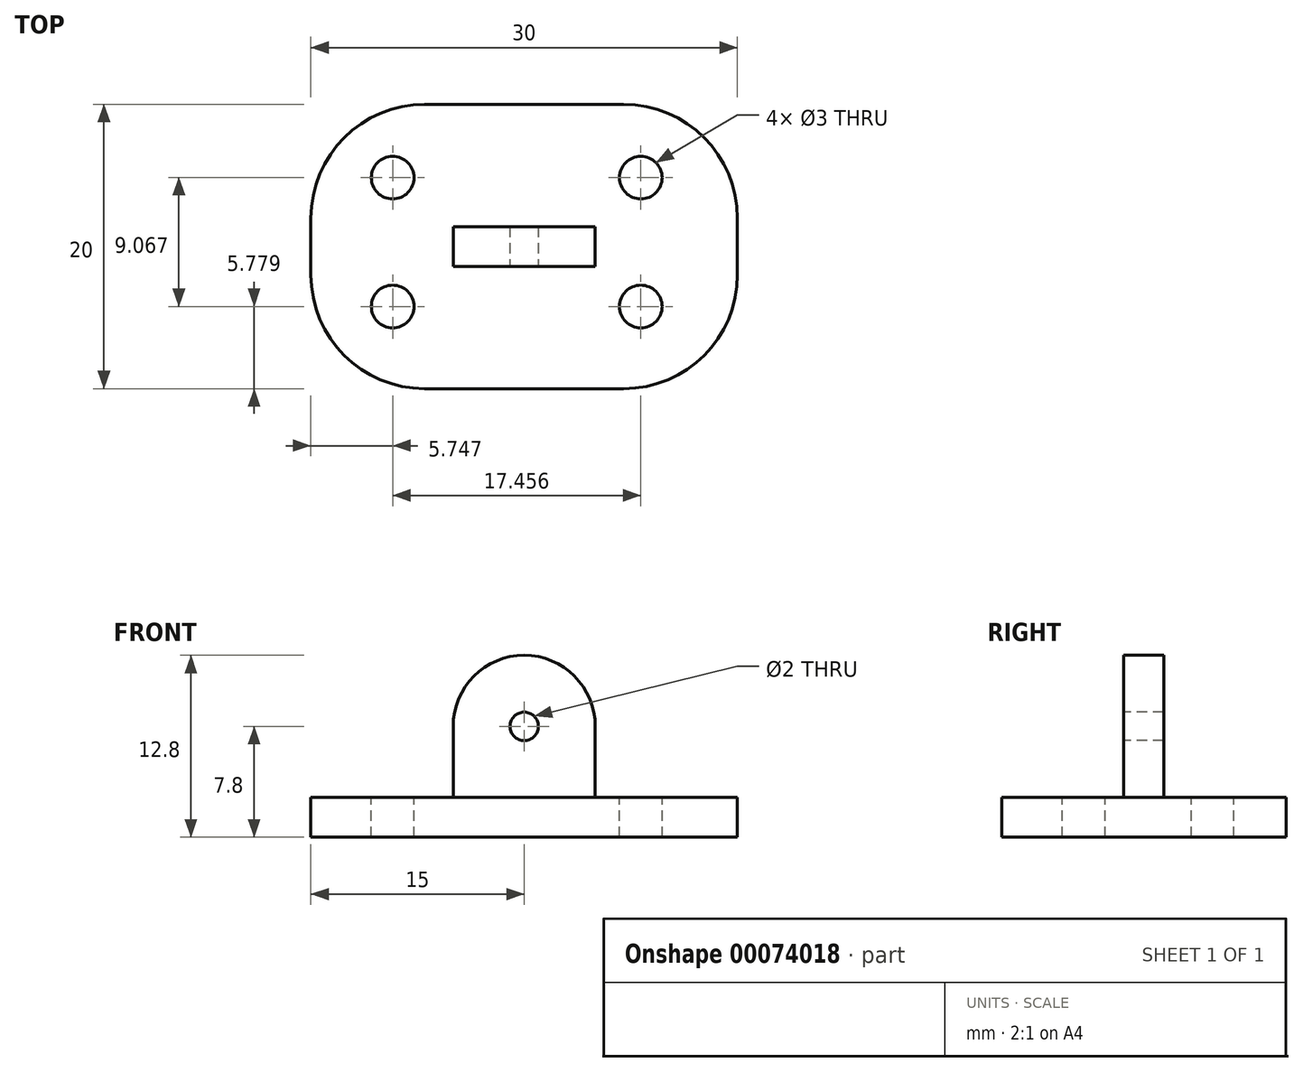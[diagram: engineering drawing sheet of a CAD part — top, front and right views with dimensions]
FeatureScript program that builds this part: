
annotation { "Feature Type Name" : "Feature", "Feature Type Description" : "" }
export const myFeature = defineFeature(function(context is Context, id is Id, definition is map)
    precondition{}
    {
        {
            var Q0;
            Q0=qCreatedBy(makeId("Top.planeOp"),FACE);
            var sketch = newSketch(context, id + "F0", { "sketchPlane" : qUnion([Q0])});
            skLineSegment(sketch, "E0.bottom", {"start": v(0, 0) * mm, "end": v(30, 0) * mm});
            skLineSegment(sketch, "E0.top", {"start": v(0, 20) * mm, "end": v(30, 20) * mm});
            skLineSegment(sketch, "E0.left", {"start": v(0, 0) * mm, "end": v(0, 20) * mm});
            skLineSegment(sketch, "E0.right", {"start": v(30, 0) * mm, "end": v(30, 20) * mm});
            skLineSegment(sketch, "E1.bottom", {"start": v(12.5, 11.4) * mm, "end": v(17.5, 11.4) * mm});
            skLineSegment(sketch, "E1.top", {"start": v(12.5, 8.6) * mm, "end": v(17.5, 8.6) * mm});
            skLineSegment(sketch, "E1.left", {"start": v(12.5, 11.4) * mm, "end": v(12.5, 8.6) * mm});
            skLineSegment(sketch, "E1.right", {"start": v(17.5, 11.4) * mm, "end": v(17.5, 8.6) * mm});
            skPoint(sketch, "E2", {"position": v(15, 20) * mm});
            skPoint(sketch, "E3", {"position": v(15, 11.4) * mm});
            skPoint(sketch, "E4", {"position": v(17.5, 10) * mm});
            skPoint(sketch, "E5", {"position": v(30, 10) * mm});
            skSolve(sketch);
        }
        {
            var Q0;
            Q0 = qSketchRegion(id + "F0", true);
            extrude(context, id + "F1", {"entities" : qUnion([Q0]), "depth" : 2.8 * mm, "offsetDistance" : 25 * mm});
        }
        {
            var Q0;
            Q0=makeQuery(id+"F1.opExtrude","CAP_FACE",FACE,{"disambiguationData":[OSD([sQuery(id+"F0.wireOp",EDGE,"E0.bottom"),sQuery(id+"F0.wireOp",EDGE,"E0.top"),sQuery(id+"F0.wireOp",EDGE,"E0.left"),sQuery(id+"F0.wireOp",EDGE,"E0.right"),sQuery(id+"F0.wireOp",EDGE,"E1.bottom"),sQuery(id+"F0.wireOp",EDGE,"E1.top"),sQuery(id+"F0.wireOp",EDGE,"E1.left"),sQuery(id+"F0.wireOp",EDGE,"E1.right")])],"isStart":false});
            var sketch = newSketch(context, id + "F2", { "sketchPlane" : qUnion([Q0])});
            skLineSegment(sketch, "E6.bottom", {"start": v(10, 11.4) * mm, "end": v(20, 11.4) * mm});
            skLineSegment(sketch, "E6.top", {"start": v(10, 8.6) * mm, "end": v(20, 8.6) * mm});
            skLineSegment(sketch, "E6.left", {"start": v(10, 11.4) * mm, "end": v(10, 8.6) * mm});
            skLineSegment(sketch, "E6.right", {"start": v(20, 11.4) * mm, "end": v(20, 8.6) * mm});
            skPoint(sketch, "E7", {"position": v(15, 11.4) * mm});
            skSolve(sketch);
        }
        {
            var Q0;
            {var subQ2=sQuery(id+"F2.wireOp",EDGE,"E6.right");Q0=makeQuery(id+"F2.imprint","IMPRINT",FACE,{"disambiguationData":[TD([[makeQuery(id+"F2.imprint","IMPRINT",EDGE,{"derivedFrom":subQ2}),-1.0]])]});}
            var Q1;
            {var subQ1=makeQuery(id+"F1.opExtrude","CAP_EDGE",EDGE,{"disambiguationData":[OSD([sQuery(id+"F0.wireOp",EDGE,"E1.left")])],"isStart":false});Q1=makeQuery(id+"F2.imprint","IMPRINT",FACE,{"disambiguationData":[TD([[makeQuery(id+"F2.imprint","IMPRINT",EDGE,{"derivedFrom":subQ1}),1.0]])]});}
            var Q2;
            {var subQ2=sQuery(id+"F2.wireOp",EDGE,"E6.left");Q2=makeQuery(id+"F2.imprint","IMPRINT",FACE,{"disambiguationData":[TD([[makeQuery(id+"F2.imprint","IMPRINT",EDGE,{"derivedFrom":subQ2}),1.0]])]});}
            extrude(context, id + "F3", {"entities" : qUnion([Q0, Q1, Q2]), "depth" : 10 * mm, "offsetDistance" : 25 * mm});
        }
        {
            var Q0;
            Q0=makeQuery(id+"F3.opExtrude","SWEPT_FACE",FACE,{"disambiguationData":[OSD([sQuery(id+"F2.wireOp",EDGE,"E6.top")])]});
            var sketch = newSketch(context, id + "F4", { "sketchPlane" : qUnion([Q0])});
            skPoint(sketch, "E8", {"position": v(15, 7.8) * mm});
            skSolve(sketch);
        }
        {
            var Q0;
            Q0=sQuery(id+"F4.wireOp",VERTEX,"E8");
            var Q1;
            Q1=makeQuery(id+"F3.opExtrude","SWEPT_BODY",BODY,{"disambiguationData":[OSD([sQuery(id+"F2.wireOp",EDGE,"E6.bottom"),sQuery(id+"F2.wireOp",EDGE,"E6.top"),sQuery(id+"F2.wireOp",EDGE,"E6.left"),sQuery(id+"F2.wireOp",EDGE,"E6.right")])]});
            hole(context, id + "F5", {"style" : HoleStyle.SIMPLE, "endStyle" : HoleEndStyle.THROUGH, "holeDiameter" : 2 * mm, "majorDiameter" : 5 * mm, "tappedDepth" : 12 * mm, "tapClearance" : 3, "locations" : qUnion([Q0]), "scope" : qUnion([Q1])});
        }
        {
            var Q0;
            Q0=makeQuery(id+"F3.opExtrude","CAP_EDGE",EDGE,{"disambiguationData":[OSD([sQuery(id+"F2.wireOp",EDGE,"E6.left")])],"isStart":false});
            var Q1;
            Q1=makeQuery(id+"F3.opExtrude","CAP_EDGE",EDGE,{"disambiguationData":[OSD([sQuery(id+"F2.wireOp",EDGE,"E6.right")])],"isStart":false});
            fillet(context, id + "F6", {"entities" : qUnion([Q0, Q1]), "tangentPropagation" : true, "radius" : 5 * mm, "defaultsChanged" : false, "vertexSettings" : [], "allowEdgeOverflow" : false});
        }
        {
            var Q0;
            Q0=makeQuery(id+"F3.opExtrude","CAP_FACE",FACE,{"disambiguationData":[OSD([sQuery(id+"F2.wireOp",EDGE,"E6.bottom"),sQuery(id+"F2.wireOp",EDGE,"E6.top"),sQuery(id+"F2.wireOp",EDGE,"E6.left"),sQuery(id+"F2.wireOp",EDGE,"E6.right")])],"isStart":true});
            var sketch = newSketch(context, id + "F7", { "sketchPlane" : qUnion([Q0])});
            skLineSegment(sketch, "E9.bottom", {"start": v(12.5, -8.6) * mm, "end": v(17.5, -8.6) * mm});
            skLineSegment(sketch, "E9.top", {"start": v(12.5, -11.4) * mm, "end": v(17.5, -11.4) * mm});
            skLineSegment(sketch, "E9.left", {"start": v(12.5, -8.6) * mm, "end": v(12.5, -11.4) * mm});
            skLineSegment(sketch, "E9.right", {"start": v(17.5, -8.6) * mm, "end": v(17.5, -11.4) * mm});
            skPoint(sketch, "E10", {"position": v(15, -11.4) * mm});
            skPoint(sketch, "E11", {"position": v(17.5, -10) * mm});
            skSolve(sketch);
        }
        {
            var Q0;
            Q0=makeQuery(id+"F7.imprint","IMPRINT",FACE,{"disambiguationData":[TD([[makeQuery(id+"F7.imprint","IMPRINT",EDGE,{"derivedFrom":sQuery(id+"F7.wireOp",EDGE,"E9.bottom")}),-1.0]])]});
            extrude(context, id + "F8", {"entities" : qUnion([Q0]), "operationType" : NewBodyOperationType.ADD, "depth" : 2.8 * mm, "offsetDistance" : 25 * mm});
        }
        {
            var Q0;
            Q0=makeQuery(id+"F1.opExtrude","SWEPT_EDGE",EDGE,{"disambiguationData":[OSD([sQuery(id+"F0.wireOp",EDGE,"E0.top"),sQuery(id+"F0.wireOp",EDGE,"E0.right")])]});
            var Q1;
            Q1=makeQuery(id+"F1.opExtrude","SWEPT_EDGE",EDGE,{"disambiguationData":[OSD([sQuery(id+"F0.wireOp",EDGE,"E0.top"),sQuery(id+"F0.wireOp",EDGE,"E0.left")])]});
            var Q2;
            Q2=makeQuery(id+"F1.opExtrude","SWEPT_EDGE",EDGE,{"disambiguationData":[OSD([sQuery(id+"F0.wireOp",EDGE,"E0.bottom"),sQuery(id+"F0.wireOp",EDGE,"E0.right")])]});
            var Q3;
            Q3=makeQuery(id+"F1.opExtrude","SWEPT_EDGE",EDGE,{"disambiguationData":[OSD([sQuery(id+"F0.wireOp",EDGE,"E0.bottom"),sQuery(id+"F0.wireOp",EDGE,"E0.left")])]});
            fillet(context, id + "F9", {"entities" : qUnion([Q0, Q1, Q2, Q3]), "tangentPropagation" : true, "radius" : 8 * mm, "defaultsChanged" : true, "vertexSettings" : [], "allowEdgeOverflow" : false});
        }
        {
            var Q0;
            Q0=makeQuery(id+"F1.opExtrude","CAP_FACE",FACE,{"disambiguationData":[OSD([sQuery(id+"F0.wireOp",EDGE,"E0.bottom"),sQuery(id+"F0.wireOp",EDGE,"E0.top"),sQuery(id+"F0.wireOp",EDGE,"E0.left"),sQuery(id+"F0.wireOp",EDGE,"E0.right"),sQuery(id+"F0.wireOp",EDGE,"E1.bottom"),sQuery(id+"F0.wireOp",EDGE,"E1.top"),sQuery(id+"F0.wireOp",EDGE,"E1.left"),sQuery(id+"F0.wireOp",EDGE,"E1.right")])],"isStart":false});
            var sketch = newSketch(context, id + "F10", { "sketchPlane" : qUnion([Q0])});
            skPoint(sketch, "E12", {"position": v(5.75, 14.85) * mm});
            skPoint(sketch, "E13", {"position": v(5.75, 5.78) * mm});
            skPoint(sketch, "E14", {"position": v(23.2, 14.85) * mm});
            skPoint(sketch, "E15", {"position": v(23.2, 5.78) * mm});
            skSolve(sketch);
        }
        {
            var Q0;
            Q0=sQuery(id+"F10.wireOp",VERTEX,"E12");
            var Q1;
            Q1=sQuery(id+"F10.wireOp",VERTEX,"E14");
            var Q2;
            Q2=sQuery(id+"F10.wireOp",VERTEX,"E15");
            var Q3;
            Q3=sQuery(id+"F10.wireOp",VERTEX,"E13");
            var Q4;
            Q4=makeQuery(id+"F1.opExtrude","SWEPT_BODY",BODY,{"disambiguationData":[OSD([sQuery(id+"F0.wireOp",EDGE,"E0.bottom"),sQuery(id+"F0.wireOp",EDGE,"E0.top"),sQuery(id+"F0.wireOp",EDGE,"E0.left"),sQuery(id+"F0.wireOp",EDGE,"E0.right"),sQuery(id+"F0.wireOp",EDGE,"E1.bottom"),sQuery(id+"F0.wireOp",EDGE,"E1.top"),sQuery(id+"F0.wireOp",EDGE,"E1.left"),sQuery(id+"F0.wireOp",EDGE,"E1.right")])]});
            hole(context, id + "F11", {"style" : HoleStyle.SIMPLE, "endStyle" : HoleEndStyle.THROUGH, "holeDiameter" : 3 * mm, "majorDiameter" : 5 * mm, "tappedDepth" : 12 * mm, "tapClearance" : 3, "locations" : qUnion([Q0, Q1, Q2, Q3]), "scope" : qUnion([Q4])});
        }
    });
